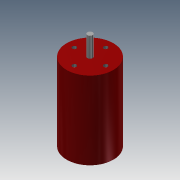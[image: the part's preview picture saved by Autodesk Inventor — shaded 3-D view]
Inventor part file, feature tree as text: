
AUTODESK INVENTOR PART (.ipt)
format: ipt  version: 2013 (Build 170138000, 138)  size: 95,232 bytes
history: native  units: mm
features: sketch x3, extrude x2, hole x1
ambient origin geometry x8: Origin, YZ Plane, XZ Plane, XY Plane, X Axis, Y Axis, Z Axis, Center Point
bodies: Solid1 (feature_tree)
feature tree (6):
  extrude  "Extrusion1"  Depth=47.0mm TaperAngle=0.0deg
  extrude  "Extrusion2"  Depth=12.0mm TaperAngle=0.0deg
  hole  "Hole1"  [1 undecoded]
  sketch  "Sketch1"  dims[d0=28.2mm d1=47.0mm d2=0.0mm]
  sketch  "Sketch2"  dims[d3=3.17mm d4=12.0mm d5=0.0mm]
  sketch  "Sketch3"  dims[d8=2.4mm d9=2.4mm d10=2.4mm d11=2.4mm d12=2.459mm d13=3.0mm d14=4.0mm d15=2.0mm d16=90.0deg d17=3.0mm d18=0.0mm]
note: 1 required parameter value undecoded (feature->parameter linkage not recoverable at this tier; creation-order binding heuristic only, values carry confidence <= 0.55)
